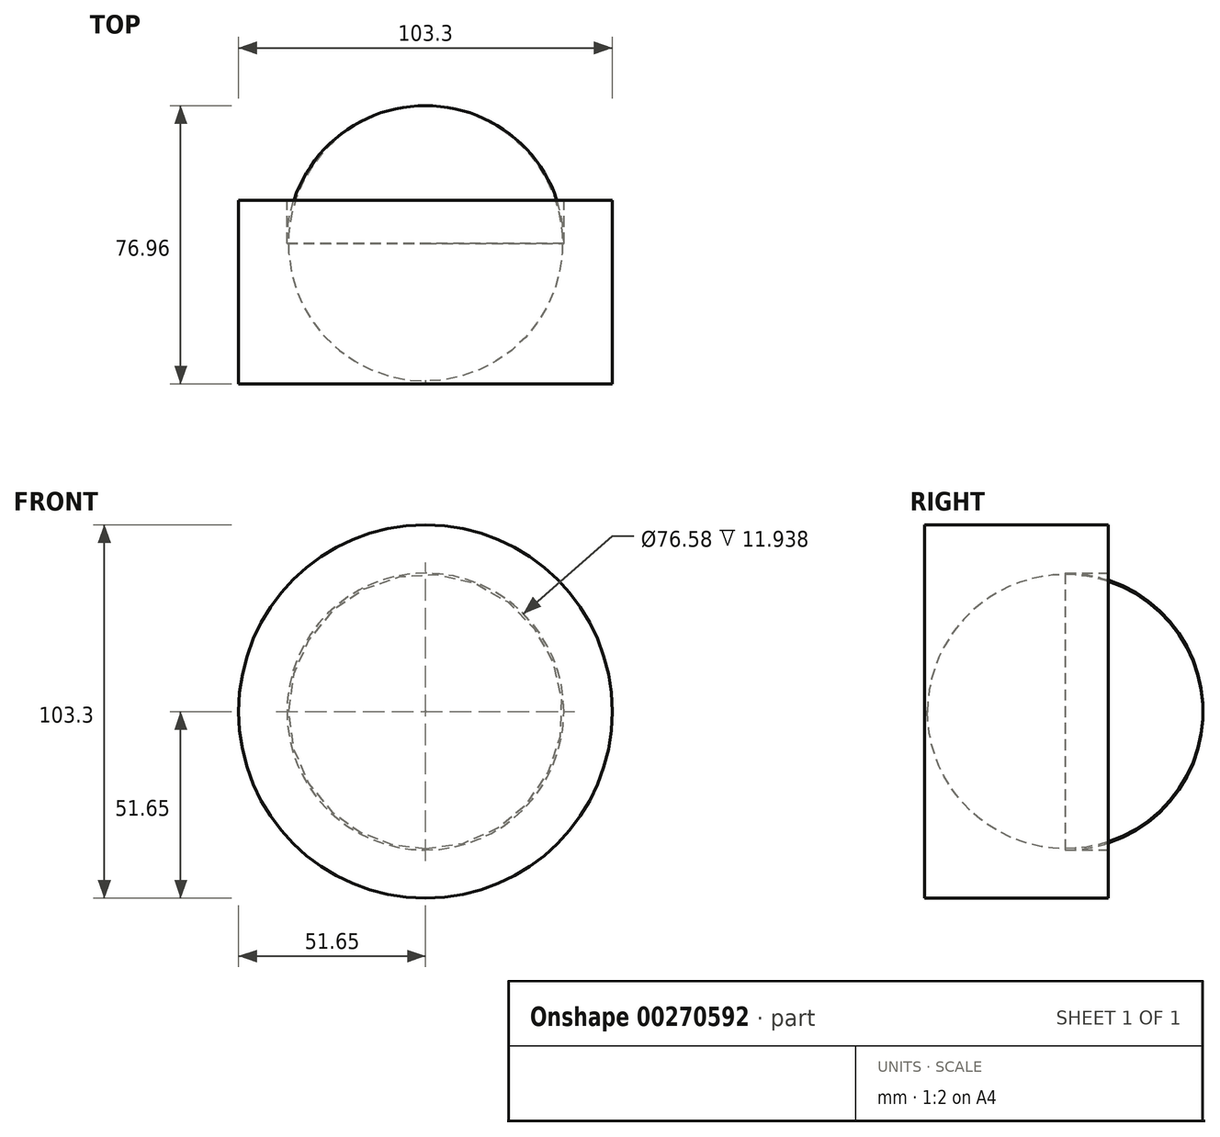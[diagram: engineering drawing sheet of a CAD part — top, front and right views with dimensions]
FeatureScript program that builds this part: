
annotation { "Feature Type Name" : "Feature", "Feature Type Description" : "" }
export const myFeature = defineFeature(function(context is Context, id is Id, definition is map)
    precondition{}
    {
        {
            var Q0;
            Q0=qCreatedBy(makeId("Front.planeOp"),FACE);
            var sketch = newSketch(context, id + "F0", { "sketchPlane" : qUnion([Q0])});
            skCircle(sketch, "E0", {"center": v(0, 0) * mm, "radius": 51.65 * mm});
            skSolve(sketch);
        }
        {
            var Q0;
            Q0 = qSketchRegion(id + "F0", true);
            extrude(context, id + "F1", {"entities" : qUnion([Q0]), "depth" : 50.8 * mm});
        }
        {
            var Q0;
            Q0=makeQuery(id+"F1.opExtrude","CAP_FACE",FACE,{"disambiguationData":[OSD([sQuery(id+"F0.wireOp",EDGE,"E0")])],"isStart":true});
            var sketch = newSketch(context, id + "F2", { "sketchPlane" : qUnion([Q0])});
            skCircle(sketch, "E1", {"center": v(0, 0) * mm, "radius": 38.3 * mm});
            skSolve(sketch);
        }
        {
            var Q0;
            Q0=makeQuery(id+"F2.imprint","IMPRINT",FACE,{"disambiguationData":[TD([[makeQuery(id+"F2.imprint","IMPRINT",EDGE,{"derivedFrom":sQuery(id+"F2.wireOp",EDGE,"E1")}),1.0]])]});
            extrude(context, id + "F3", {"entities" : qUnion([Q0]), "operationType" : NewBodyOperationType.REMOVE, "oppositeDirection" : true, "depth" : 50.04 * mm});
        }
        {
            var Q0;
            Q0=makeQuery(id+"F3.boolean.opBoolean","COPY",EDGE,{"derivedFrom":makeQuery(id+"F3.opExtrude","CAP_EDGE",EDGE,{"disambiguationData":[OSD([sQuery(id+"F2.wireOp",EDGE,"E1")])],"isStart":false})});
            fillet(context, id + "F4", {"entities" : qUnion([Q0]), "radius" : 38.1 * mm, "tangentPropagation" : true, "allowEdgeOverflow" : false});
        }
    });
